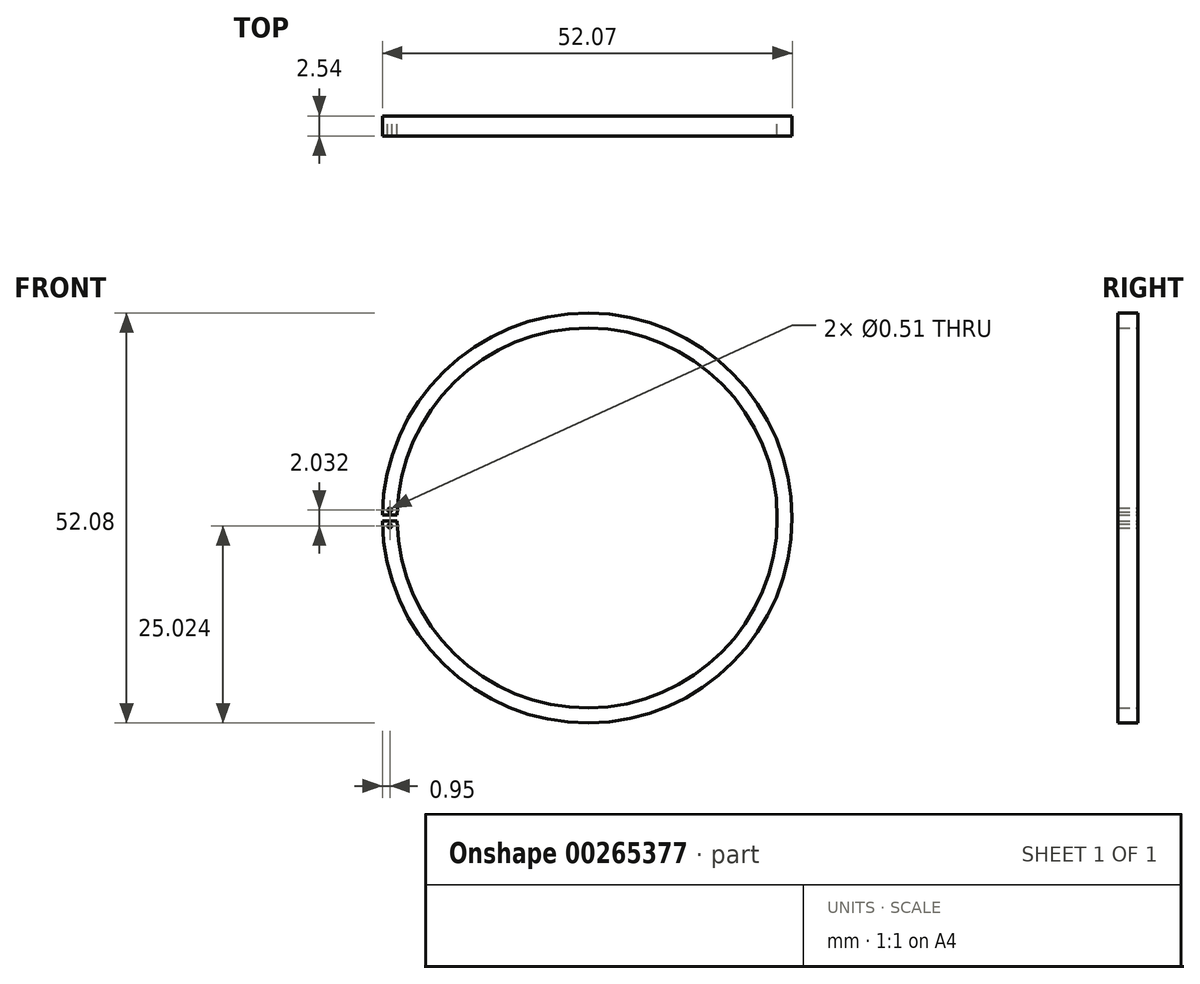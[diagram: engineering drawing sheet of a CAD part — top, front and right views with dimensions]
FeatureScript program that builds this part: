
annotation { "Feature Type Name" : "Feature", "Feature Type Description" : "" }
export const myFeature = defineFeature(function(context is Context, id is Id, definition is map)
    precondition{}
    {
        {
            var Q0;
            Q0=qCreatedBy(makeId("Front.planeOp"),FACE);
            var sketch = newSketch(context, id + "F0", { "sketchPlane" : qUnion([Q0])});
            skCircle(sketch, "E0", {"center": v(0, 0) * mm, "radius": 26.04 * mm});
            skCircle(sketch, "E1", {"center": v(0, 0) * mm, "radius": 24.13 * mm});
            skSolve(sketch);
        }
        {
            var Q0;
            Q0=makeQuery(id+"F0.imprint","IMPRINT",FACE,{"disambiguationData":[TD([[makeQuery(id+"F0.imprint","IMPRINT",EDGE,{"derivedFrom":sQuery(id+"F0.wireOp",EDGE,"E0")}),1.0]])]});
            extrude(context, id + "F1", {"entities" : qUnion([Q0]), "depth" : 2.54 * mm, "symmetric" : true});
        }
        {
            var Q0;
            Q0=qCreatedBy(makeId("Front.planeOp"),FACE);
            var sketch = newSketch(context, id + "F2", { "sketchPlane" : qUnion([Q0])});
            skArc(sketch, "E2.0", {"start": v(-26.03, 0.38) * mm, "mid": v(-26.04, 0) * mm, "end": v(-26.03, -0.38) * mm});
            skArc(sketch, "E3.0", {"start": v(-24.13, 0.38) * mm, "mid": v(-24.13, 0) * mm, "end": v(-24.13, -0.38) * mm});
            skLineSegment(sketch, "E4", {"start": v(-26.03, 0.38) * mm, "end": v(-24.13, 0.38) * mm});
            skLineSegment(sketch, "E5", {"start": v(-26.03, -0.38) * mm, "end": v(-24.13, -0.38) * mm});
            skCircle(sketch, "E6", {"center": v(-25.08, -1.02) * mm, "radius": 0.25 * mm});
            skPoint(sketch, "E6.centerSnap0", {"position": v(-25.08, -0.38) * mm});
            skCircle(sketch, "E7", {"center": v(-25.08, 1.02) * mm, "radius": 0.25 * mm});
            skPoint(sketch, "E7.centerSnap0", {"position": v(-25.08, 0.38) * mm});
            skSolve(sketch);
        }
        {
            var Q0;
            Q0 = qSketchRegion(id + "F2", true);
            extrude(context, id + "F3", {"entities" : qUnion([Q0]), "operationType" : NewBodyOperationType.REMOVE, "depth" : 25.4 * mm, "symmetric" : true});
        }
    });
